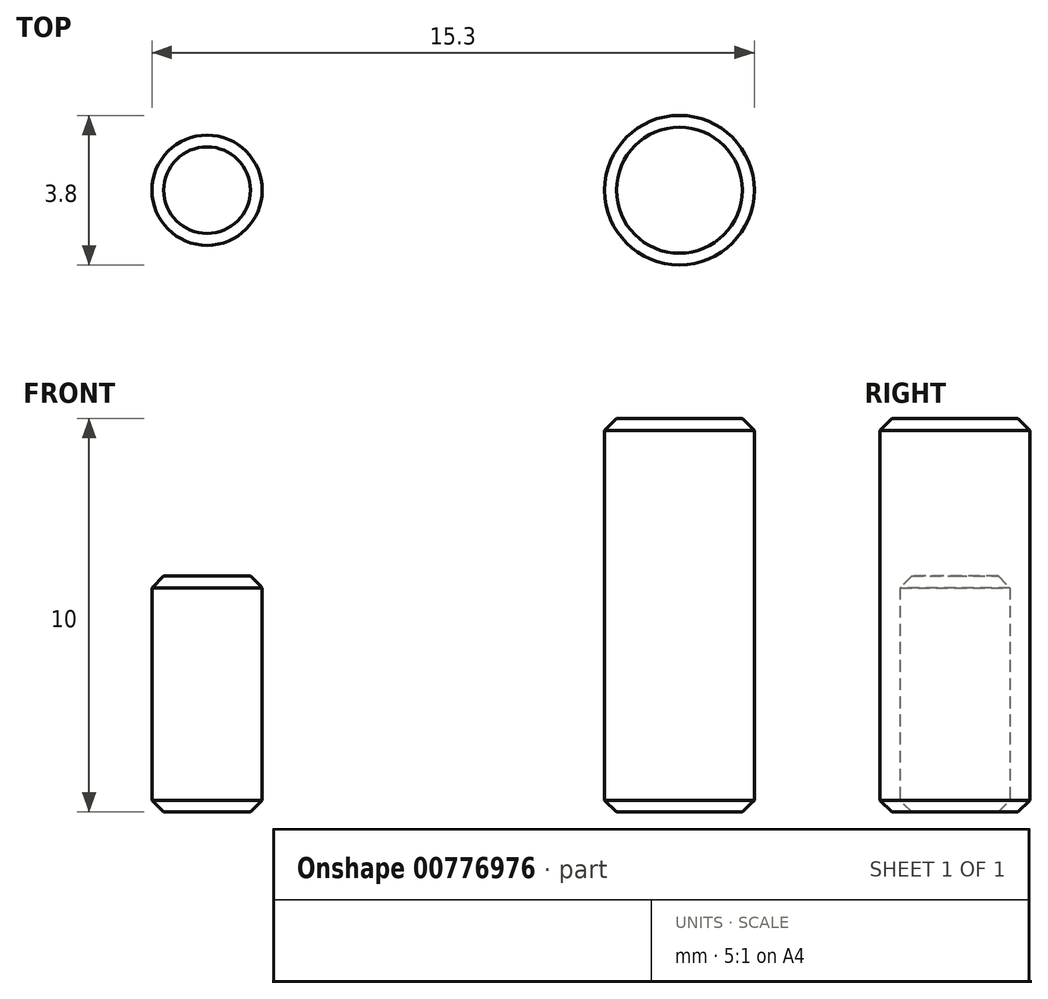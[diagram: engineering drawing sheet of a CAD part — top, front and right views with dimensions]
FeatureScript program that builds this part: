
annotation { "Feature Type Name" : "Feature", "Feature Type Description" : "" }
export const myFeature = defineFeature(function(context is Context, id is Id, definition is map)
    precondition{}
    {
        {
            var Q0;
            Q0=qCreatedBy(makeId("Top.planeOp"),FACE);
            var sketch = newSketch(context, id + "F0", { "sketchPlane" : qUnion([Q0])});
            skCircle(sketch, "E0", {"center": v(0, 0) * mm, "radius": 1.4 * mm});
            skCircle(sketch, "E1", {"center": v(12, 0) * mm, "radius": 1.9 * mm});
            skLineSegment(sketch, "E2", {"start": v(0, 0) * mm, "end": v(12, 0) * mm, "construction": true});
            skLineSegment(sketch, "E3", {"start": v(0, 0) * mm, "end": v(0, 1.4) * mm, "construction": true});
            skSolve(sketch);
        }
        {
            var Q0;
            {var subQ0=sQuery(id+"F0.wireOp",EDGE,"E1");var subQ1=makeQuery(id+"F0.imprint","INTERSECT",VERTEX,{"derivedFrom":[subQ0,sQuery(id+"F0.wireOp",EDGE,"biekJW3f-CqpC-7gmu-4ArM-MwDc2peyGsgI")]});Q0=makeQuery(id+"F0.imprint","IMPRINT",FACE,{"disambiguationData":[TD([[makeQuery(id+"F0.imprint","IMPRINT",EDGE,{"disambiguationData":[TD([[subQ1,-1.0]])],"derivedFrom":subQ0}),1.0]])]});}
            extrude(context, id + "F1", {"entities" : qUnion([Q0]), "depth" : 10 * mm, "offsetDistance" : 25 * mm});
        }
        {
            var Q0;
            Q0=makeQuery(id+"F0.imprint","IMPRINT",FACE,{"disambiguationData":[TD([[makeQuery(id+"F0.imprint","IMPRINT",EDGE,{"derivedFrom":sQuery(id+"F0.wireOp",EDGE,"E0")}),1.0]])]});
            extrude(context, id + "F2", {"entities" : qUnion([Q0]), "depth" : 6 * mm, "offsetDistance" : 25 * mm});
        }
        {
            var Q0;
            Q0=makeQuery(id+"F1.opExtrude","CAP_FACE",FACE,{"disambiguationData":[OSD([sQuery(id+"F0.wireOp",EDGE,"E0")])],"isStart":false});
            var Q1;
            Q1=makeQuery(id+"F1.opExtrude","CAP_FACE",FACE,{"disambiguationData":[OSD([sQuery(id+"F0.wireOp",EDGE,"E1")])],"isStart":false});
            var Q2;
            Q2=makeQuery(id+"F1.opExtrude","CAP_FACE",FACE,{"disambiguationData":[OSD([sQuery(id+"F0.wireOp",EDGE,"E0")])],"isStart":true});
            var Q3;
            Q3=makeQuery(id+"F1.opExtrude","CAP_FACE",FACE,{"disambiguationData":[OSD([sQuery(id+"F0.wireOp",EDGE,"E1")])],"isStart":true});
            var Q4;
            Q4=makeQuery(id+"F2.opExtrude","CAP_FACE",FACE,{"disambiguationData":[OSD([sQuery(id+"F0.wireOp",EDGE,"E0")])],"isStart":false});
            var Q5;
            Q5=makeQuery(id+"F2.opExtrude","CAP_FACE",FACE,{"disambiguationData":[OSD([sQuery(id+"F0.wireOp",EDGE,"E0")])],"isStart":true});
            chamfer(context, id + "F3", {"entities" : qUnion([Q0, Q1, Q2, Q3, Q4, Q5]), "width" : 0.3 * mm, "tangentPropagation" : true});
        }
    });
